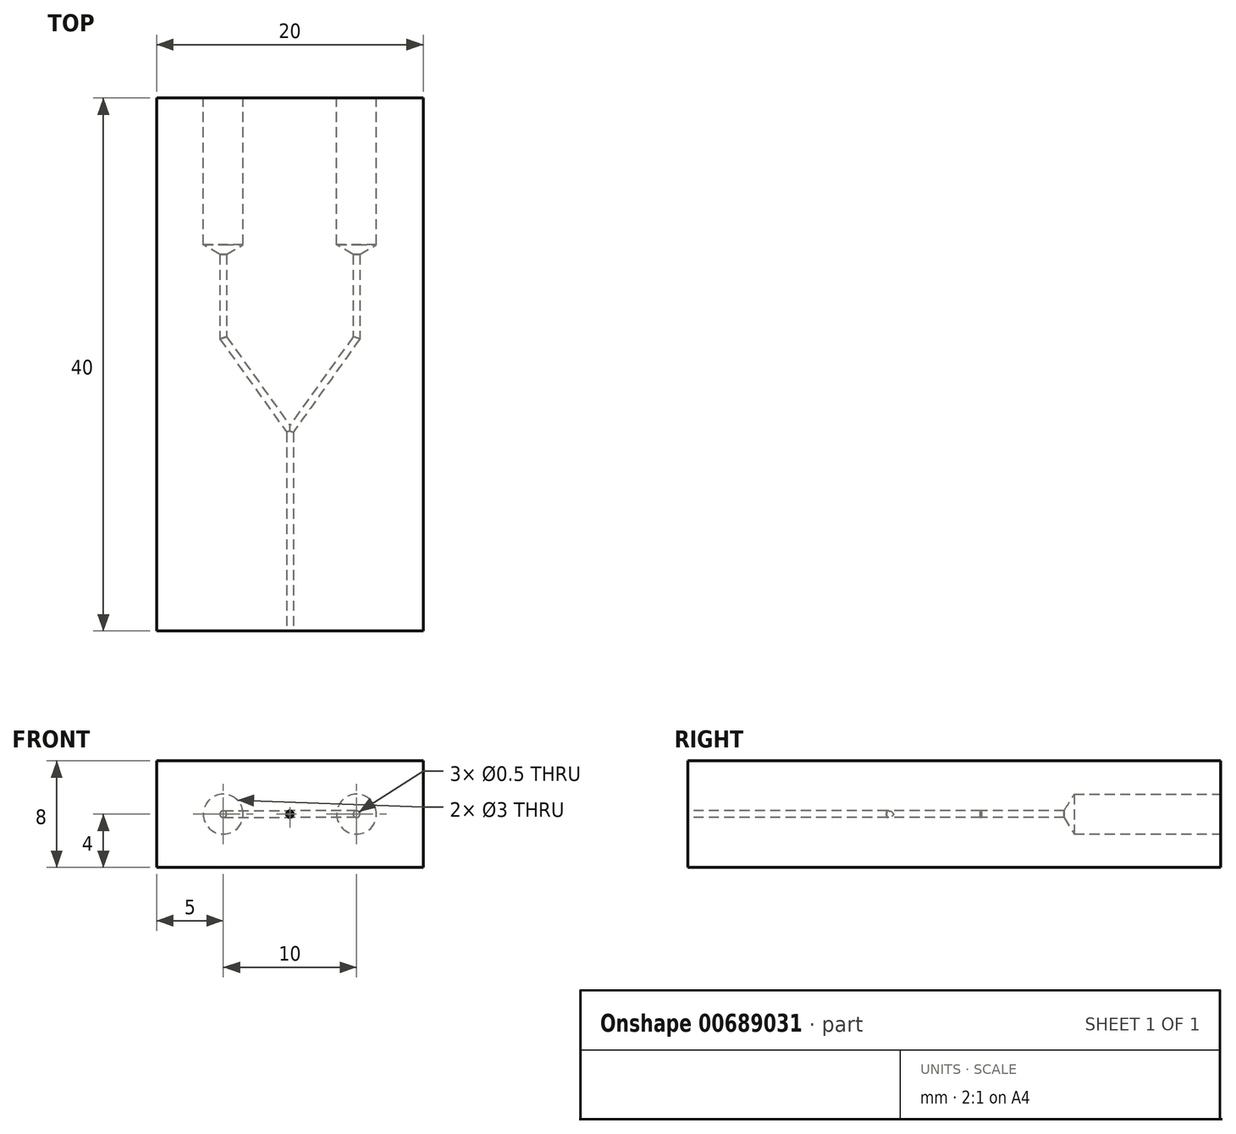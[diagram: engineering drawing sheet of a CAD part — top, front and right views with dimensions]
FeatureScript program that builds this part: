
annotation { "Feature Type Name" : "Feature", "Feature Type Description" : "" }
export const myFeature = defineFeature(function(context is Context, id is Id, definition is map)
    precondition{}
    {
        {
            var Q0;
            Q0=qCreatedBy(makeId("Top.planeOp"),FACE);
            var sketch = newSketch(context, id + "F0", { "sketchPlane" : qUnion([Q0])});
            skLineSegment(sketch, "E0.bottom", {"start": v(10, 20) * mm, "end": v(-10, 20) * mm});
            skLineSegment(sketch, "E0.top", {"start": v(10, -20) * mm, "end": v(-10, -20) * mm});
            skLineSegment(sketch, "E0.left", {"start": v(10, 20) * mm, "end": v(10, -20) * mm});
            skLineSegment(sketch, "E0.right", {"start": v(-10, 20) * mm, "end": v(-10, -20) * mm});
            skPoint(sketch, "E0.middle", {"position": v(0, 0) * mm});
            skSolve(sketch);
        }
        {
            var Q0;
            Q0 = qSketchRegion(id + "F0", true);
            extrude(context, id + "F1", {"entities" : qUnion([Q0]), "depth" : 4 * mm, "offsetDistance" : 25 * mm, "hasSecondDirection" : true, "secondDirectionOppositeDirection" : true, "secondDirectionDepth" : 4 * mm});
        }
        {
            var Q0;
            Q0=qCreatedBy(makeId("Top.planeOp"),FACE);
            var sketch = newSketch(context, id + "F2", { "sketchPlane" : qUnion([Q0])});
            skLineSegment(sketch, "E1", {"start": v(0, -20) * mm, "end": v(0, -5) * mm});
            skLineSegment(sketch, "E2", {"start": v(0, -5) * mm, "end": v(5, -5) * mm, "construction": true});
            skLineSegment(sketch, "E3", {"start": v(5, -5) * mm, "end": v(5, 2) * mm, "construction": true});
            skLineSegment(sketch, "E4", {"start": v(0, -5) * mm, "end": v(5, 2) * mm});
            skLineSegment(sketch, "E5", {"start": v(5, 2) * mm, "end": v(5, 20) * mm});
            skSolve(sketch);
        }
        {
            var Q0;
            Q0=makeQuery(id+"F1.opExtrude","SWEPT_FACE",FACE,{"disambiguationData":[OSD([sQuery(id+"F0.wireOp",EDGE,"E0.bottom")])]});
            var sketch = newSketch(context, id + "F3", { "sketchPlane" : qUnion([Q0])});
            skCircle(sketch, "E6", {"center": v(-5, 0) * mm, "radius": 0.25 * mm});
            skSolve(sketch);
        }
        {
            var Q0;
            Q0 = qSketchRegion(id + "F3", true);
            var Q1;
            Q1 = qConstructionFilter(qBodyType(qCreatedBy(id + "F2" ,EDGE), BodyType.WIRE), ConstructionObject.NO);
            sweep(context, id + "F4", {"operationType" : NewBodyOperationType.REMOVE, "profiles" : qUnion([Q0]), "path" : qUnion([Q1])});
        }
        {
            var Q0;
            Q0=qCreatedBy(makeId("Top.planeOp"),FACE);
            var sketch = newSketch(context, id + "F5", { "sketchPlane" : qUnion([Q0])});
            skLineSegment(sketch, "E7", {"start": v(0, -20) * mm, "end": v(0, -5) * mm, "construction": true});
            skLineSegment(sketch, "E8", {"start": v(0, -5) * mm, "end": v(-5, -5) * mm, "construction": true});
            skLineSegment(sketch, "E9", {"start": v(-5, -5) * mm, "end": v(-5, 2) * mm, "construction": true});
            skLineSegment(sketch, "E10", {"start": v(0, -5) * mm, "end": v(-5, 2) * mm});
            skLineSegment(sketch, "E11", {"start": v(-5, 2) * mm, "end": v(-5, 20) * mm});
            skSolve(sketch);
        }
        {
            var Q0;
            Q0=makeQuery(id+"F1.opExtrude","SWEPT_FACE",FACE,{"disambiguationData":[OSD([sQuery(id+"F0.wireOp",EDGE,"E0.bottom")])]});
            var sketch = newSketch(context, id + "F6", { "sketchPlane" : qUnion([Q0])});
            skCircle(sketch, "E12", {"center": v(5, 0) * mm, "radius": 0.25 * mm});
            skSolve(sketch);
        }
        {
            var Q0;
            Q0 = qSketchRegion(id + "F6", true);
            var Q1;
            Q1 = qConstructionFilter(qBodyType(qCreatedBy(id + "F5" ,EDGE), BodyType.WIRE), ConstructionObject.NO);
            sweep(context, id + "F7", {"operationType" : NewBodyOperationType.REMOVE, "profiles" : qUnion([Q0]), "path" : qUnion([Q1])});
        }
        {
            var Q0;
            Q0=makeQuery(id+"F1.opExtrude","SWEPT_FACE",FACE,{"disambiguationData":[OSD([sQuery(id+"F0.wireOp",EDGE,"E0.bottom")])]});
            var sketch = newSketch(context, id + "F8", { "sketchPlane" : qUnion([Q0])});
            skPoint(sketch, "E13", {"position": v(-5, 0) * mm});
            skSolve(sketch);
        }
        {
            var Q0;
            {var subQ0=sQuery(id+"F0.wireOp",EDGE,"E0.bottom");Q0=makeQuery(id+"F8.imprint","IMPRINT",FACE,{"disambiguationData":[TD([[makeQuery(id+"F8.imprint","IMPRINT",EDGE,{"derivedFrom":makeQuery(id+"F1.opExtrude","CAP_EDGE",EDGE,{"disambiguationData":[OSD([subQ0])],"isStart":true})}),1.0]])]});}
            var sketch = newSketch(context, id + "F9", { "sketchPlane" : qUnion([Q0])});
            skPoint(sketch, "E14", {"position": v(5, 0) * mm});
            skSolve(sketch);
        }
        {
            var Q0;
            Q0=sQuery(id+"F8.wireOp",VERTEX,"E13");
            var Q1;
            Q1=makeQuery(id+"F1.opExtrude","SWEPT_BODY",BODY,{"disambiguationData":[OSD([sQuery(id+"F0.wireOp",EDGE,"E0.bottom"),sQuery(id+"F0.wireOp",EDGE,"E0.top"),sQuery(id+"F0.wireOp",EDGE,"E0.left"),sQuery(id+"F0.wireOp",EDGE,"E0.right")])]});
            hole(context, id + "F10", {"style" : HoleStyle.SIMPLE, "endStyle" : HoleEndStyle.BLIND, "holeDiameter" : 3 * mm, "majorDiameter" : 5 * mm, "holeDepth" : 11 * mm, "isTappedThrough" : true, "tappedDepth" : 12 * mm, "tapClearance" : 3, "locations" : qUnion([Q0]), "scope" : qUnion([Q1])});
        }
        {
            var Q0;
            Q0=sQuery(id+"F9.wireOp",VERTEX,"E14");
            var Q1;
            Q1=makeQuery(id+"F1.opExtrude","SWEPT_BODY",BODY,{"disambiguationData":[OSD([sQuery(id+"F0.wireOp",EDGE,"E0.bottom"),sQuery(id+"F0.wireOp",EDGE,"E0.top"),sQuery(id+"F0.wireOp",EDGE,"E0.left"),sQuery(id+"F0.wireOp",EDGE,"E0.right")])]});
            hole(context, id + "F11", {"style" : HoleStyle.SIMPLE, "endStyle" : HoleEndStyle.BLIND, "holeDiameter" : 3 * mm, "majorDiameter" : 5 * mm, "holeDepth" : 11 * mm, "isTappedThrough" : true, "tappedDepth" : 12 * mm, "tapClearance" : 3, "locations" : qUnion([Q0]), "scope" : qUnion([Q1])});
        }
    });
